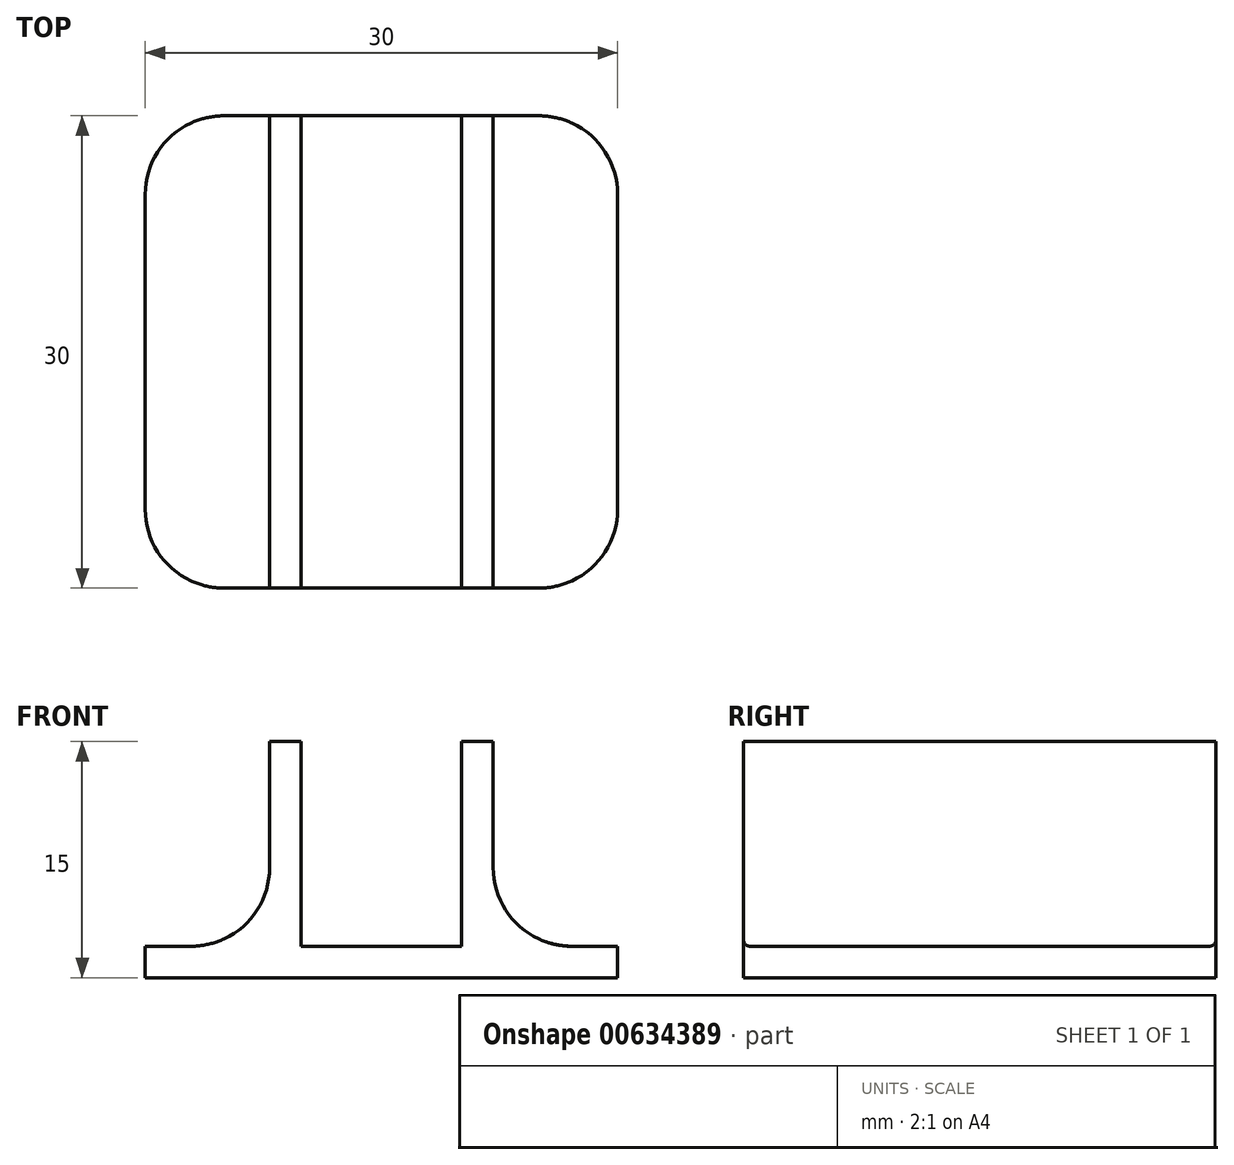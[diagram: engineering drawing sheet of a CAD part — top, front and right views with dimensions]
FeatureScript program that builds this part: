
annotation { "Feature Type Name" : "Feature", "Feature Type Description" : "" }
export const myFeature = defineFeature(function(context is Context, id is Id, definition is map)
    precondition{}
    {
        {
            var Q0;
            Q0=qCreatedBy(makeId("Front.planeOp"),FACE);
            var sketch = newSketch(context, id + "F0", { "sketchPlane" : qUnion([Q0])});
            skLineSegment(sketch, "E0", {"start": v(-15, 0) * mm, "end": v(15, 0) * mm});
            skLineSegment(sketch, "E1", {"start": v(15, 0) * mm, "end": v(15, 2) * mm});
            skLineSegment(sketch, "E2", {"start": v(15, 2) * mm, "end": v(7.1, 2) * mm});
            skLineSegment(sketch, "E3", {"start": v(7.1, 2) * mm, "end": v(7.1, 15) * mm});
            skLineSegment(sketch, "E4", {"start": v(7.1, 15) * mm, "end": v(5.1, 15) * mm});
            skLineSegment(sketch, "E5", {"start": v(5.1, 15) * mm, "end": v(5.1, 2) * mm});
            skLineSegment(sketch, "E6", {"start": v(5.1, 2) * mm, "end": v(-5.1, 2) * mm});
            skLineSegment(sketch, "E7", {"start": v(-5.1, 2) * mm, "end": v(-5.1, 15) * mm});
            skLineSegment(sketch, "E8", {"start": v(-5.1, 15) * mm, "end": v(-7.1, 15) * mm});
            skLineSegment(sketch, "E9", {"start": v(-7.1, 15) * mm, "end": v(-7.1, 2) * mm});
            skLineSegment(sketch, "E10", {"start": v(-7.1, 2) * mm, "end": v(-15, 2) * mm});
            skLineSegment(sketch, "E11", {"start": v(-15, 2) * mm, "end": v(-15, 0) * mm});
            skLineSegment(sketch, "E12", {"start": v(0, 0) * mm, "end": v(0, 2) * mm, "construction": true});
            skSolve(sketch);
        }
        {
            var Q0;
            Q0=makeQuery(id+"F0.imprint","IMPRINT",FACE,{"disambiguationData":[TD([[makeQuery(id+"F0.imprint","IMPRINT",EDGE,{"derivedFrom":sQuery(id+"F0.wireOp",EDGE,"E0")}),1.0]])]});
            extrude(context, id + "F1", {"entities" : qUnion([Q0]), "oppositeDirection" : true, "depth" : 30 * mm, "offsetDistance" : 25 * mm});
        }
        {
            var Q0;
            Q0=makeQuery(id+"F1.opExtrude","CAP_EDGE",EDGE,{"disambiguationData":[OSD([sQuery(id+"F0.wireOp",EDGE,"E11")])],"isStart":true});
            var Q1;
            Q1=makeQuery(id+"F1.opExtrude","CAP_EDGE",EDGE,{"disambiguationData":[OSD([sQuery(id+"F0.wireOp",EDGE,"E1")])],"isStart":true});
            var Q2;
            Q2=makeQuery(id+"F1.opExtrude","CAP_EDGE",EDGE,{"disambiguationData":[OSD([sQuery(id+"F0.wireOp",EDGE,"E11")])],"isStart":false});
            var Q3;
            Q3=makeQuery(id+"F1.opExtrude","CAP_EDGE",EDGE,{"disambiguationData":[OSD([sQuery(id+"F0.wireOp",EDGE,"E1")])],"isStart":false});
            fillet(context, id + "F2", {"entities" : qUnion([Q0, Q1, Q2, Q3]), "radius" : 5 * mm, "tangentPropagation" : true, "allowEdgeOverflow" : false});
        }
        {
            var Q0;
            Q0=makeQuery(id+"F1.opExtrude","SWEPT_EDGE",EDGE,{"disambiguationData":[OSD([sQuery(id+"F0.wireOp",EDGE,"E9"),sQuery(id+"F0.wireOp",EDGE,"E10")])]});
            var Q1;
            Q1=makeQuery(id+"F1.opExtrude","SWEPT_EDGE",EDGE,{"disambiguationData":[OSD([sQuery(id+"F0.wireOp",EDGE,"E2"),sQuery(id+"F0.wireOp",EDGE,"E3")])]});
            fillet(context, id + "F3", {"entities" : qUnion([Q0, Q1]), "radius" : 5 * mm, "tangentPropagation" : true, "allowEdgeOverflow" : false});
        }
    });
